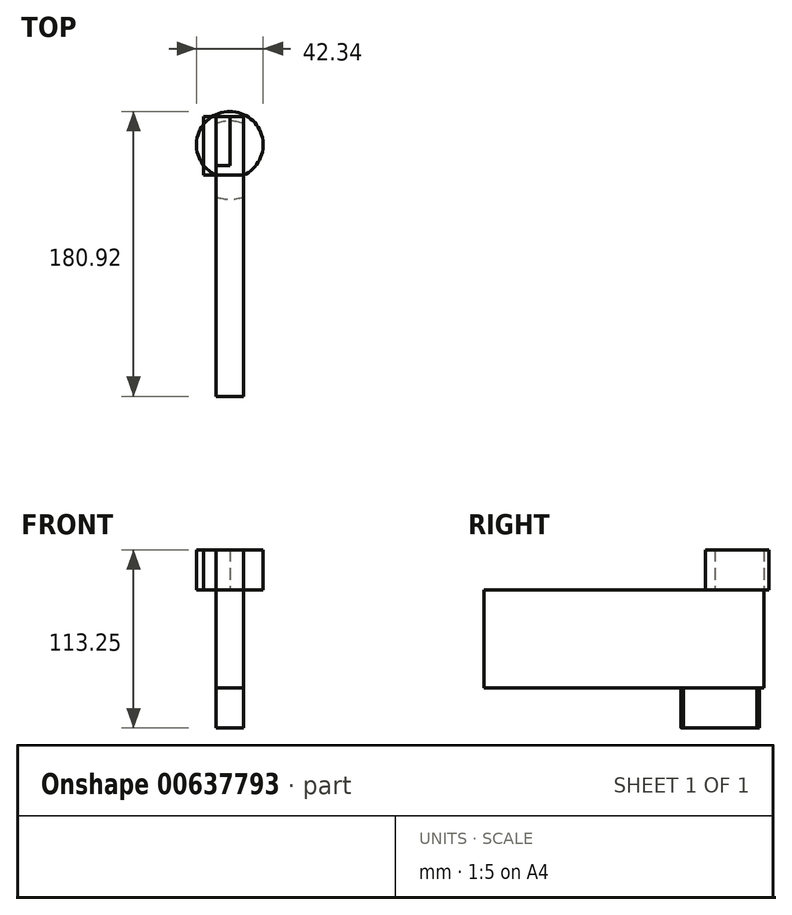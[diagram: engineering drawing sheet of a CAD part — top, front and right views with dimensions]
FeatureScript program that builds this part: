
annotation { "Feature Type Name" : "Feature", "Feature Type Description" : "" }
export const myFeature = defineFeature(function(context is Context, id is Id, definition is map)
    precondition{}
    {
        {
            var Q0;
            Q0=qCreatedBy(makeId("Front.planeOp"),FACE);
            var sketch = newSketch(context, id + "F0", { "sketchPlane" : qUnion([Q0])});
            skLineSegment(sketch, "E0.bottom", {"start": v(-55.28, 48.03) * mm, "end": v(-37.9, 48.03) * mm});
            skLineSegment(sketch, "E0.top", {"start": v(-55.28, -14.42) * mm, "end": v(-37.9, -14.42) * mm});
            skLineSegment(sketch, "E0.left", {"start": v(-55.28, 48.03) * mm, "end": v(-55.28, -14.42) * mm});
            skLineSegment(sketch, "E0.right", {"start": v(-37.9, 48.03) * mm, "end": v(-37.9, -14.42) * mm});
            skSolve(sketch);
        }
        {
            var Q0;
            Q0=makeQuery(id+"F0.imprint","IMPRINT",FACE,{"disambiguationData":[TD([[makeQuery(id+"F0.imprint","IMPRINT",EDGE,{"derivedFrom":sQuery(id+"F0.wireOp",EDGE,"E0.bottom")}),-1.0]])]});
            extrude(context, id + "F1", {"entities" : qUnion([Q0]), "depth" : 127 * mm, "offsetDistance" : 25.4 * mm});
        }
        {
            var Q0;
            Q0=makeQuery(id+"F1.opExtrude","CAP_FACE",FACE,{"disambiguationData":[OSD([sQuery(id+"F0.wireOp",EDGE,"E0.bottom"),sQuery(id+"F0.wireOp",EDGE,"E0.top"),sQuery(id+"F0.wireOp",EDGE,"E0.left"),sQuery(id+"F0.wireOp",EDGE,"E0.right")])],"isStart":false});
            extrude(context, id + "F2", {"entities" : qUnion([Q0]), "operationType" : NewBodyOperationType.ADD, "depth" : 50.8 * mm, "offsetDistance" : 25.4 * mm});
        }
        {
            var Q0;
            {var subQ0=sQuery(id+"F0.wireOp",EDGE,"E0.bottom");Q0=makeQuery(id+"F2.boolean.opBoolean","MERGE",FACE,{"derivedFrom":[makeQuery(id+"F1.opExtrude","SWEPT_FACE",FACE,{"disambiguationData":[OSD([subQ0])]}),makeQuery(id+"F2.opExtrude","SWEPT_FACE",FACE,{"disambiguationData":[OSD([subQ0])]})]});}
            var sketch = newSketch(context, id + "F3", { "sketchPlane" : qUnion([Q0])});
            skCircle(sketch, "E1", {"center": v(-46.6, -18.05) * mm, "radius": 21.17 * mm});
            skPoint(sketch, "E1.centerSnap0", {"position": v(-46.6, 0) * mm});
            skSolve(sketch);
        }
        {
            var Q0;
            {var subQ2=sQuery(id+"F0.wireOp",EDGE,"E0.bottom");var subQ8=makeQuery(id+"F1.opExtrude","CAP_EDGE",EDGE,{"disambiguationData":[OSD([subQ2])],"isStart":true});Q0=makeQuery(id+"F3.imprint","IMPRINT",FACE,{"disambiguationData":[TD([[makeQuery(id+"F3.imprint","IMPRINT",EDGE,{"derivedFrom":subQ8}),1.0]])]});}
            extrude(context, id + "F4", {"entities" : qUnion([Q0]), "depth" : 25.4 * mm, "offsetDistance" : 25.4 * mm});
        }
        {
            var Q0;
            {var subQ0=sQuery(id+"F0.wireOp",EDGE,"E0.top");Q0=makeQuery(id+"F2.boolean.opBoolean","MERGE",FACE,{"derivedFrom":[makeQuery(id+"F1.opExtrude","SWEPT_FACE",FACE,{"disambiguationData":[OSD([subQ0])]}),makeQuery(id+"F2.opExtrude","SWEPT_FACE",FACE,{"disambiguationData":[OSD([subQ0])]})]});}
            var sketch = newSketch(context, id + "F5", { "sketchPlane" : qUnion([Q0])});
            skCircle(sketch, "E2", {"center": v(-46.6, 27.81) * mm, "radius": 24.8 * mm});
            skSolve(sketch);
        }
        {
            var Q0;
            {var subQ0=sQuery(id+"F5.wireOp",EDGE,"E2");var subQ1=sQuery(id+"F0.wireOp",EDGE,"E0.right");var subQ2=sQuery(id+"F0.wireOp",EDGE,"E0.top");var subQ3=makeQuery(id+"F2.boolean.opBoolean","MERGE",EDGE,{"derivedFrom":[makeQuery(id+"F1.opExtrude","SWEPT_EDGE",EDGE,{"disambiguationData":[OSD([subQ2,subQ1])]}),makeQuery(id+"F2.opExtrude","SWEPT_EDGE",EDGE,{"disambiguationData":[OSD([subQ2,subQ1])]})]});var subQ4=makeQuery(id+"F5.imprint","INTERSECT",VERTEX,{"disambiguationData":[OD(0.0)],"derivedFrom":[subQ3,subQ0]});Q0=makeQuery(id+"F5.imprint","IMPRINT",FACE,{"disambiguationData":[TD([[makeQuery(id+"F5.imprint","IMPRINT",EDGE,{"disambiguationData":[TD([[subQ4,1.0]])],"derivedFrom":subQ0}),1.0]])]});}
            extrude(context, id + "F6", {"entities" : qUnion([Q0]), "depth" : 25.4 * mm, "offsetDistance" : 25.4 * mm});
        }
        {
            var Q0;
            {var subQ0=sQuery(id+"F0.wireOp",EDGE,"E0.bottom");Q0=makeQuery(id+"F2.boolean.opBoolean","MERGE",FACE,{"derivedFrom":[makeQuery(id+"F1.opExtrude","SWEPT_FACE",FACE,{"disambiguationData":[OSD([subQ0])]}),makeQuery(id+"F2.opExtrude","SWEPT_FACE",FACE,{"disambiguationData":[OSD([subQ0])]})]});}
            var sketch = newSketch(context, id + "F7", { "sketchPlane" : qUnion([Q0])});
            skLineSegment(sketch, "E3.bottom", {"start": v(-37.9, -31.13) * mm, "end": v(-46.6, -31.13) * mm});
            skLineSegment(sketch, "E3.top", {"start": v(-37.9, 0) * mm, "end": v(-46.6, 0) * mm});
            skLineSegment(sketch, "E3.left", {"start": v(-37.9, -31.13) * mm, "end": v(-37.9, 0) * mm});
            skLineSegment(sketch, "E3.right", {"start": v(-46.6, -31.13) * mm, "end": v(-46.6, 0) * mm});
            skLineSegment(sketch, "E4.bottom", {"start": v(-37.9, -31.13) * mm, "end": v(-55.28, -31.13) * mm});
            skLineSegment(sketch, "E4.top", {"start": v(-37.9, 0) * mm, "end": v(-55.28, 0) * mm});
            skLineSegment(sketch, "E4.right", {"start": v(-55.28, -31.13) * mm, "end": v(-55.28, 0) * mm});
            skSolve(sketch);
        }
        {
            var Q0;
            {var subQ0=sQuery(id+"F7.wireOp",EDGE,"E3.right");Q0=makeQuery(id+"F7.imprint","IMPRINT",FACE,{"disambiguationData":[TD([[makeQuery(id+"F7.imprint","IMPRINT",EDGE,{"derivedFrom":subQ0}),1.0]])]});}
            extrude(context, id + "F8", {"entities" : qUnion([Q0]), "depth" : 25.4 * mm, "offsetDistance" : 25.4 * mm});
        }
        {
            var Q0;
            Q0=makeQuery(id+"F4.opExtrude","SWEPT_FACE",FACE,{"disambiguationData":[OSD([sQuery(id+"F0.wireOp",EDGE,"E0.bottom"),sQuery(id+"F0.wireOp",EDGE,"E0.right")])]});
            extrude(context, id + "F9", {"entities" : qUnion([Q0]), "depth" : 25.4 * mm, "offsetDistance" : 25.4 * mm});
        }
    });
